# Revit family: EVID-C8.2LP
name_source: partatom
category: Communication Devices
revit_build: Autodesk Revit 2017 (Build: 20160225_1515(x64)
units: mm (PartAtom-declared; Revit-internal decimal feet)

## family parameters
Always vertical = Yes
Cut with Voids When Loaded = No
Maintain Annotation Orientation = Yes
OmniClass Number = 23.85.10.11.11.21
OmniClass Title = Speakers
Part Type = Normal
Room Calculation Point = No
Round Connector Dimension = Use Diameter
Shared = No
Work Plane-Based = Yes

## types (1)
- EVIDC8.2LP_Ceiling_Speaker_Pair
    ArchitectsAndEngineersSpecs = https://www.electrovoice.com
    BackLength = 238 mm  [stored 0.78084 ft]
    CTN = EVIDC8.2LP
    Default Elevation = 0 mm  [stored 0 ft]
    Depth = 218 mm  [stored 0.715223 ft]
    Description = Low Profile 8" coaxial two-way. Waveguide coupled Ti Tweeter. Full bandwith overload protection. Front baffle wattage tap adjustment. Integrated low loss matching transformer allows for either 70v/100v or 8-ohm operation. Includes tile bridge and mounting ring for easy installation. Integrated ported enclosure for extended bass reponse. Ideal for ceiling spaces with tight clearance.
    Disclaimer = http://resource.boschsecurity.com
    FrontLength = 300 mm
    Height = 218 mm  [stored 0.715223 ft]
    IfcExportAs = IfcBuildingElementProxy
    IfcExportType = IfcBuildingElementProxyType
    InstallationManual = https://www.electrovoice.com
    Manufacturer = Electro Voice
    ManufacturerURL = https://www.electrovoice.com
    MaterialRALColour = RAL9010
    ModelNumber = F.01U.117.606
    ProductInformation = https://www.electrovoice.com
    Uniclass2015Code = Pr_60_75_08_02
    Version = 1

note: [stored X ft] marks values corroborated as IEEE doubles in the binary element streams (Revit-internal decimal feet)

## geometry (parser evidence)
native form markers: Blend x2, Sweep x5
no freeform markers — native parametric forms only
